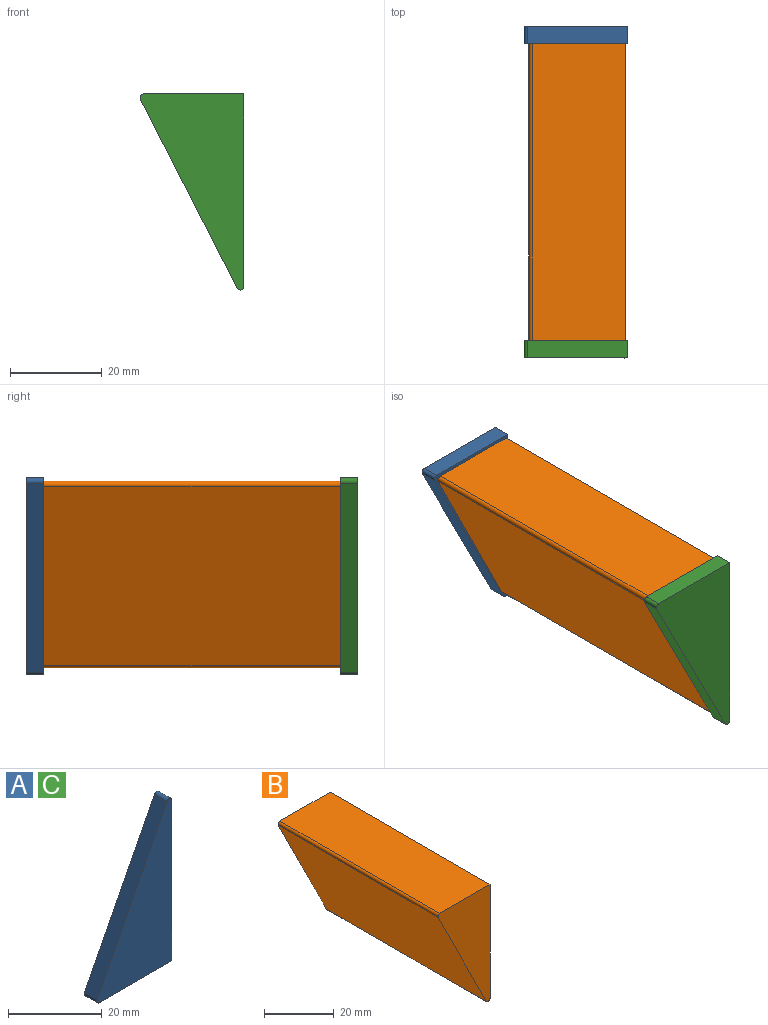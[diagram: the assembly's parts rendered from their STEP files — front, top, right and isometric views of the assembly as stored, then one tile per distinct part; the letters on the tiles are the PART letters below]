
ASSEMBLY  parts=3 mates=2
PART A: 7 faces, bbox 22.7x3.8x42.8 mm
  f0: plane 21.92x3.81mm, normal (0,0,-1), area 83.5mm2, adj f1,f3,f4,f6
  f1: plane 42.05x3.81mm, normal (1,0,0), area 160.2mm2, adj f0,f3,f4,f5
  f2: plane 41.29x21.15mm, normal (-0.89,0,0.46), area 176.8mm2, adj f3,f4,f5,f6
  f3: plane 42.82x22.68mm, normal (0,-1,0), area 521.6mm2, adj f0,f1,f2,f5,f6
  f4: plane 42.82x22.68mm, normal (0,1,0), area 521.6mm2, adj f0,f1,f2,f5,f6
  f5: cylinder r=0.76mm len=3.81mm, axis (0,1,0), area 7.7mm2, adj f1,f2,f3,f4
  f6: cylinder r=0.76mm len=3.81mm, axis (0,1,0), area 5.9mm2, adj f0,f2,f3,f4
PART B: 7 faces, bbox 21.1x64.8x40.7 mm
  f0: plane 64.77x39.95mm, normal (1,0,0), area 2587.4mm2, adj f1,f3,f4,f5
  f1: plane 64.77x20.32mm, normal (0,0,1), area 1316.2mm2, adj f0,f3,f4,f6
  f2: plane 64.77x39.19mm, normal (-0.89,0,-0.45), area 2836.6mm2, adj f3,f4,f5,f6
  f3: plane 40.71x21.08mm, normal (0,-1,0), area 463.3mm2, adj f0,f1,f2,f5,f6
  f4: plane 40.71x21.08mm, normal (0,1,0), area 463.3mm2, adj f0,f1,f2,f5,f6
  f5: cylinder r=0.76mm len=64.77mm, axis (0,1,0), area 132.2mm2, adj f0,f2,f3,f4
  f6: cylinder r=0.76mm len=64.77mm, axis (0,1,0), area 100.4mm2, adj f1,f2,f3,f4
PART C: same geometry as A
PLACE A rot(axis=(1,0,0),180deg) t=(0.54,0,0.69)mm
PLACE B at identity
PLACE C rot(axis=(1,0,0),180deg) t=(0.54,-68.58,0.69)mm
MATE fastened A.f4 <-> B.f4  axis (0,-1,0) through (-7.2,0,-14.31)mm
MATE fastened C.f3 <-> B.f3  axis (0,1,0) through (-7.2,-64.77,-14.31)mm
